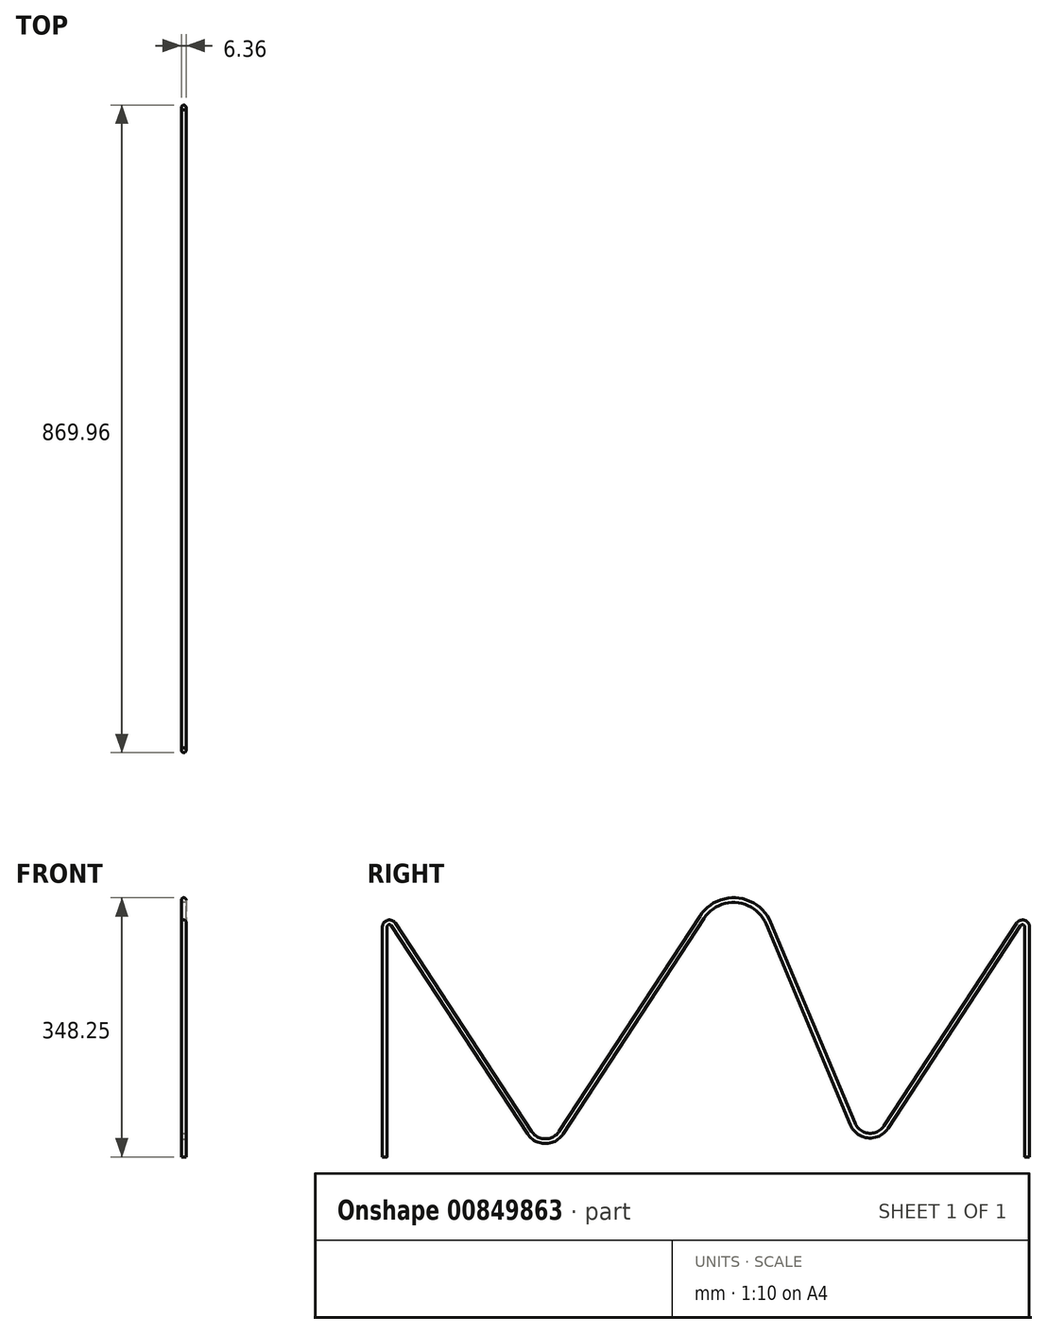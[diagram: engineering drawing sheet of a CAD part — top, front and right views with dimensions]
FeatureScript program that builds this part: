
annotation { "Feature Type Name" : "Feature", "Feature Type Description" : "" }
export const myFeature = defineFeature(function(context is Context, id is Id, definition is map)
    precondition{}
    {
        {
            var Q0;
            Q0=qCreatedBy(makeId("Right.planeOp"),FACE);
            var sketch = newSketch(context, id + "F0", { "sketchPlane" : qUnion([Q0])});
            skLineSegment(sketch, "E0", {"start": v(0, 0) * mm, "end": v(0, 308.88) * mm});
            skLineSegment(sketch, "E1", {"start": v(11.66, 312.36) * mm, "end": v(194.64, 32.51) * mm});
            skLineSegment(sketch, "E2", {"start": v(426.49, 322.07) * mm, "end": v(237.16, 32.51) * mm});
            skLineSegment(sketch, "E3", {"start": v(863.6, 0) * mm, "end": v(863.6, 308.88) * mm});
            skLineSegment(sketch, "E4", {"start": v(851.94, 312.36) * mm, "end": v(673.86, 40.01) * mm});
            skLineSegment(sketch, "E5", {"start": v(629.19, 44.08) * mm, "end": v(515.84, 313.94) * mm});
            skPoint(sketch, "E6.visualSharp", {"position": v(0, 330.2) * mm});
            skArc(sketch, "E6.filletArc", {"start": v(11.66, 312.36) * mm, "mid": v(4.54, 314.97) * mm, "end": v(0, 308.88) * mm});
            skPoint(sketch, "E7.visualSharp", {"position": v(478.81, 402.1) * mm});
            skArc(sketch, "E7.filletArc", {"start": v(515.84, 313.94) * mm, "mid": v(473.6, 344.86) * mm, "end": v(426.49, 322.07) * mm});
            skPoint(sketch, "E8.visualSharp", {"position": v(863.6, 330.2) * mm});
            skArc(sketch, "E8.filletArc", {"start": v(863.6, 308.88) * mm, "mid": v(859.06, 314.97) * mm, "end": v(851.94, 312.36) * mm});
            skPoint(sketch, "E9.visualSharp", {"position": v(215.9, 0) * mm});
            skArc(sketch, "E9.filletArc", {"start": v(194.64, 32.51) * mm, "mid": v(215.9, 21.01) * mm, "end": v(237.16, 32.51) * mm});
            skPoint(sketch, "E10.visualSharp", {"position": v(647.7, 0) * mm});
            skArc(sketch, "E10.filletArc", {"start": v(629.19, 44.08) * mm, "mid": v(650.3, 28.62) * mm, "end": v(673.86, 40.01) * mm});
            skSolve(sketch);
        }
        {
            var Q0;
            Q0=qCreatedBy(makeId("Top.planeOp"),FACE);
            var sketch = newSketch(context, id + "F1", { "sketchPlane" : qUnion([Q0])});
            skCircle(sketch, "E11", {"center": v(0, 0) * mm, "radius": 3.17 * mm});
            skSolve(sketch);
        }
        {
            var Q0;
            Q0=makeQuery(id+"F1.imprint","IMPRINT",FACE,{"disambiguationData":[TD([[makeQuery(id+"F1.imprint","IMPRINT",EDGE,{"derivedFrom":sQuery(id+"F1.wireOp",EDGE,"E11")}),1.0]])]});
            var Q1;
            Q1=sQuery(id+"F0.wireOp",EDGE,"E0");
            var Q2;
            Q2=sQuery(id+"F0.wireOp",EDGE,"E6.filletArc");
            var Q3;
            Q3=sQuery(id+"F0.wireOp",EDGE,"E1");
            var Q4;
            Q4=sQuery(id+"F0.wireOp",EDGE,"E9.filletArc");
            var Q5;
            Q5=sQuery(id+"F0.wireOp",EDGE,"E2");
            var Q6;
            Q6=sQuery(id+"F0.wireOp",EDGE,"E7.filletArc");
            var Q7;
            Q7=sQuery(id+"F0.wireOp",EDGE,"E5");
            var Q8;
            Q8=sQuery(id+"F0.wireOp",EDGE,"E10.filletArc");
            var Q9;
            Q9=sQuery(id+"F0.wireOp",EDGE,"E4");
            var Q10;
            Q10=sQuery(id+"F0.wireOp",EDGE,"E8.filletArc");
            var Q11;
            Q11=sQuery(id+"F0.wireOp",EDGE,"E3");
            sweep(context, id + "F2", {"profiles" : qUnion([Q0]), "path" : qUnion([Q1, Q2, Q3, Q4, Q5, Q6, Q7, Q8, Q9, Q10, Q11])});
        }
    });
